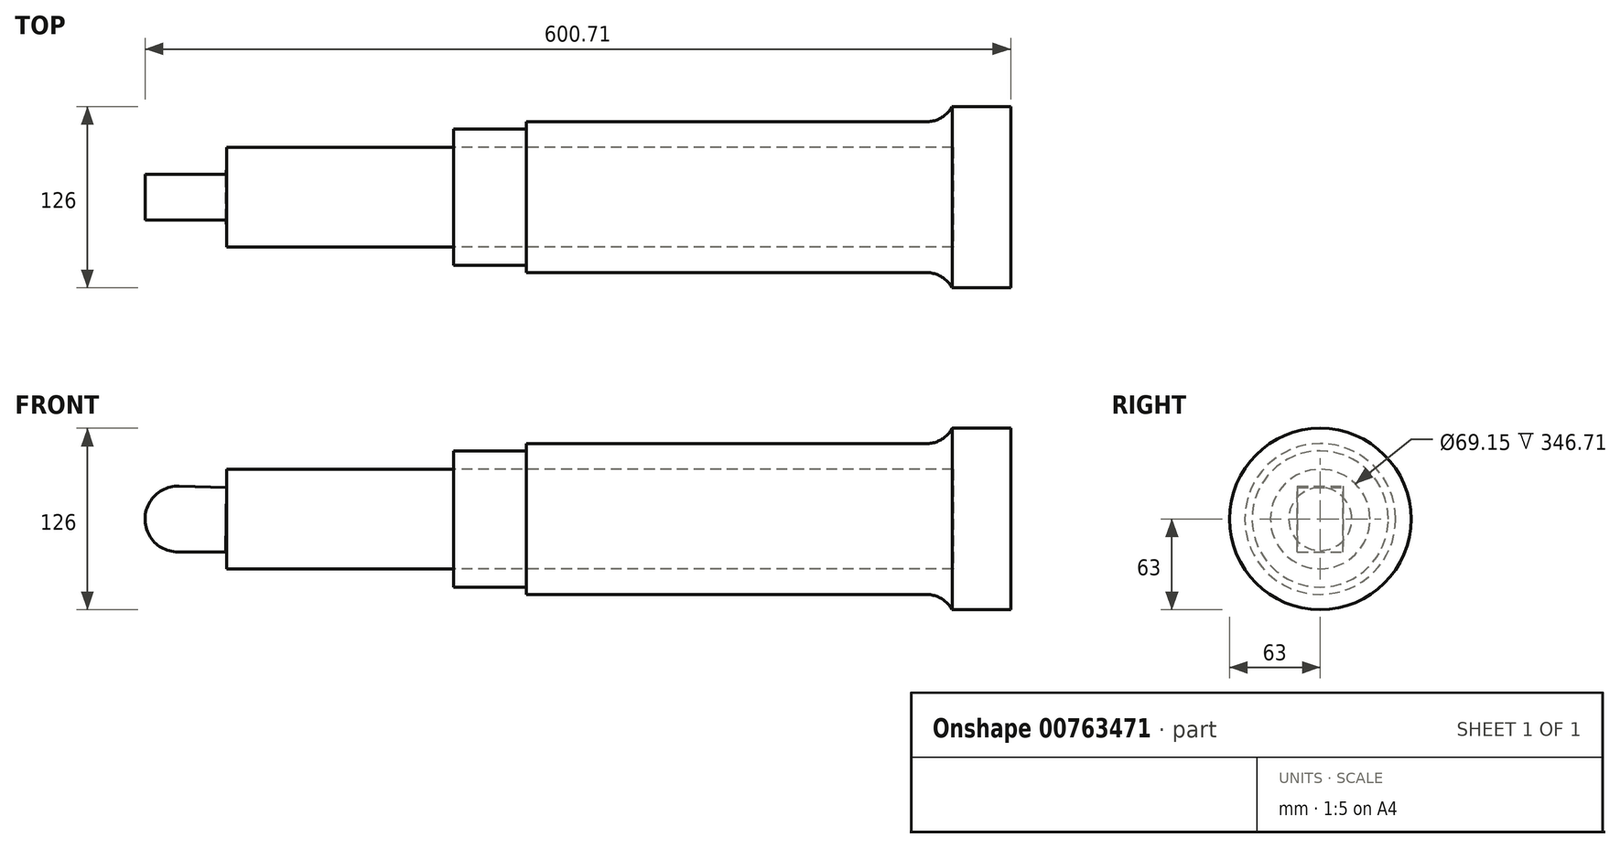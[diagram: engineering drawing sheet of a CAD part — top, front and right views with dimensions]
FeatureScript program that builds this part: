
annotation { "Feature Type Name" : "Feature", "Feature Type Description" : "" }
export const myFeature = defineFeature(function(context is Context, id is Id, definition is map)
    precondition{}
    {
        {
            var Q0;
            Q0=qCreatedBy(makeId("Front.planeOp"),FACE);
            var sketch = newSketch(context, id + "F0", { "sketchPlane" : qUnion([Q0])});
            skCircle(sketch, "E0", {"center": v(-154.2, 0) * mm, "radius": 22.86 * mm});
            skCircle(sketch, "E1", {"center": v(480.8, 0) * mm, "radius": 22.86 * mm});
            skLineSegment(sketch, "E2", {"start": v(-153.53, 22.85) * mm, "end": v(-120.5, 21.87) * mm});
            skLineSegment(sketch, "E3", {"start": v(-154.2, -22.86) * mm, "end": v(-121.18, -22.86) * mm});
            skLineSegment(sketch, "E4", {"start": v(-121.18, -22.86) * mm, "end": v(-120.5, 21.87) * mm});
            skLineSegment(sketch, "E5", {"start": v(-120.5, 21.87) * mm, "end": v(-120.5, 34.57) * mm});
            skLineSegment(sketch, "E6", {"start": v(-154.2, 0) * mm, "end": v(-120.84, 0) * mm});
            skLineSegment(sketch, "E7", {"start": v(-154.2, 0) * mm, "end": v(-154.2, -22.86) * mm});
            skLineSegment(sketch, "E8", {"start": v(-120.5, 34.57) * mm, "end": v(36.97, 34.57) * mm});
            skLineSegment(sketch, "E9", {"start": v(36.97, 34.57) * mm, "end": v(36.97, 47.27) * mm});
            skLineSegment(sketch, "E10", {"start": v(-120.84, 0) * mm, "end": v(480.8, 0) * mm});
            skLineSegment(sketch, "E11", {"start": v(480.8, -22.86) * mm, "end": v(423.65, -22.86) * mm});
            skLineSegment(sketch, "E12", {"start": v(480.8, 22.86) * mm, "end": v(423.65, 22.86) * mm});
            skLineSegment(sketch, "E13", {"start": v(423.65, -22.86) * mm, "end": v(423.65, 22.86) * mm});
            skLineSegment(sketch, "E14", {"start": v(423.65, 22.86) * mm, "end": v(423.65, 63) * mm});
            skLineSegment(sketch, "E15", {"start": v(36.97, 34.57) * mm, "end": v(383.68, 34.57) * mm});
            skLineSegment(sketch, "E16", {"start": v(383.68, 34.57) * mm, "end": v(383.68, 0) * mm});
            skLineSegment(sketch, "E17", {"start": v(423.65, 63) * mm, "end": v(383, 63) * mm});
            skLineSegment(sketch, "E18", {"start": v(36.97, 47.27) * mm, "end": v(44.6, 47.27) * mm});
            skLineSegment(sketch, "E19", {"start": v(44.6, 47.27) * mm, "end": v(87.6, 47.27) * mm});
            skLineSegment(sketch, "E20", {"start": v(87.6, 47.27) * mm, "end": v(87.6, 52.35) * mm});
            skLineSegment(sketch, "E21", {"start": v(87.6, 52.35) * mm, "end": v(365.13, 52.35) * mm});
            skLineSegment(sketch, "E22", {"start": v(382.95, 62.9) * mm, "end": v(383, 63) * mm});
            skPoint(sketch, "E23.visualSharp", {"position": v(377.16, 52.35) * mm});
            skArc(sketch, "E23.filletArc", {"start": v(365.13, 52.35) * mm, "mid": v(375.49, 55.19) * mm, "end": v(382.95, 62.9) * mm});
            skSolve(sketch);
        }
        {
            var Q0;
            Q0=makeQuery(id+"F0.imprint","IMPRINT",FACE,{"disambiguationData":[TD([[makeQuery(id+"F0.imprint","IMPRINT",EDGE,{"derivedFrom":sQuery(id+"F0.wireOp",EDGE,"E9")}),-1.0]])]});
            var Q1;
            Q1=sQuery(id+"F0.wireOp",EDGE,"E10");
            revolve(context, id + "F1", {"surfaceOperationType" : NewSurfaceOperationType.NEW, "entities" : qUnion([Q0]), "axis" : qUnion([Q1]), "revolveType" : RevolveType.FULL});
        }
        {
            var Q0;
            {var subQ4=sQuery(id+"F0.wireOp",EDGE,"E5");Q0=makeQuery(id+"F0.imprint","IMPRINT",FACE,{"disambiguationData":[TD([[makeQuery(id+"F0.imprint","IMPRINT",EDGE,{"derivedFrom":subQ4}),-1.0]])]});}
            var Q1;
            Q1=sQuery(id+"F0.wireOp",EDGE,"E10");
            revolve(context, id + "F2", {"surfaceOperationType" : NewSurfaceOperationType.NEW, "entities" : qUnion([Q0]), "axis" : qUnion([Q1]), "revolveType" : RevolveType.FULL});
        }
        {
            var Q0;
            {var subQ0=sQuery(id+"F0.wireOp",EDGE,"E2");Q0=makeQuery(id+"F0.imprint","IMPRINT",FACE,{"disambiguationData":[TD([[makeQuery(id+"F0.imprint","IMPRINT",EDGE,{"derivedFrom":subQ0}),-1.0]])]});}
            var Q1;
            {var subQ0=sQuery(id+"F0.wireOp",EDGE,"E3");Q1=makeQuery(id+"F0.imprint","IMPRINT",FACE,{"disambiguationData":[TD([[makeQuery(id+"F0.imprint","IMPRINT",EDGE,{"derivedFrom":subQ0}),1.0]])]});}
            var Q2;
            {var subQ0=sQuery(id+"F0.wireOp",EDGE,"E7");Q2=makeQuery(id+"F0.imprint","IMPRINT",FACE,{"disambiguationData":[TD([[makeQuery(id+"F0.imprint","IMPRINT",EDGE,{"derivedFrom":subQ0}),1.0]])]});}
            var Q3;
            {var subQ4=sQuery(id+"F0.wireOp",EDGE,"E7");Q3=makeQuery(id+"F0.imprint","IMPRINT",FACE,{"disambiguationData":[TD([[makeQuery(id+"F0.imprint","IMPRINT",EDGE,{"derivedFrom":subQ4}),-1.0]])]});}
            extrude(context, id + "F3", {"entities" : qUnion([Q0, Q1, Q2, Q3]), "operationType" : NewBodyOperationType.ADD, "endBound" : BoundingType.SYMMETRIC, "depth" : 31.75 * mm, "offsetDistance" : 25.4 * mm});
        }
    });
